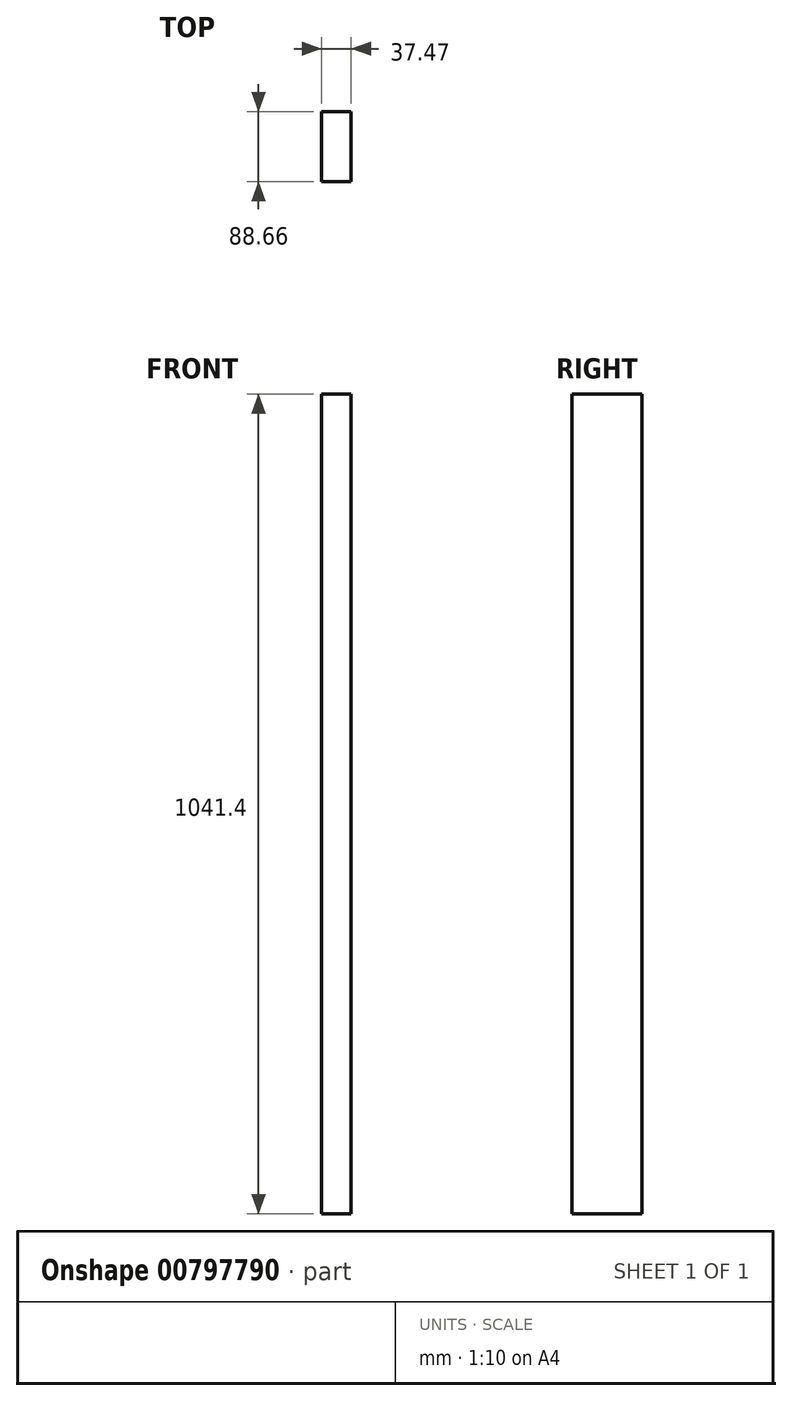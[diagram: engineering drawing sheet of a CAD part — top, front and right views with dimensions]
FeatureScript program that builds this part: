
annotation { "Feature Type Name" : "Feature", "Feature Type Description" : "" }
export const myFeature = defineFeature(function(context is Context, id is Id, definition is map)
    precondition{}
    {
        {
            var Q0;
            Q0=qCreatedBy(makeId("Top.planeOp"),FACE);
            var sketch = newSketch(context, id + "F0", { "sketchPlane" : qUnion([Q0])});
            skLineSegment(sketch, "E0.bottom", {"start": v(0, 0) * mm, "end": v(-37.47, 0) * mm});
            skLineSegment(sketch, "E0.top", {"start": v(0, 88.66) * mm, "end": v(-37.47, 88.66) * mm});
            skLineSegment(sketch, "E0.left", {"start": v(0, 0) * mm, "end": v(0, 88.66) * mm});
            skLineSegment(sketch, "E0.right", {"start": v(-37.47, 0) * mm, "end": v(-37.47, 88.66) * mm});
            skSolve(sketch);
        }
        {
            var Q0;
            Q0 = qSketchRegion(id + "F0", true);
            extrude(context, id + "F1", {"entities" : qUnion([Q0]), "depth" : 1041.4 * mm, "offsetDistance" : 25.4 * mm});
        }
    });
